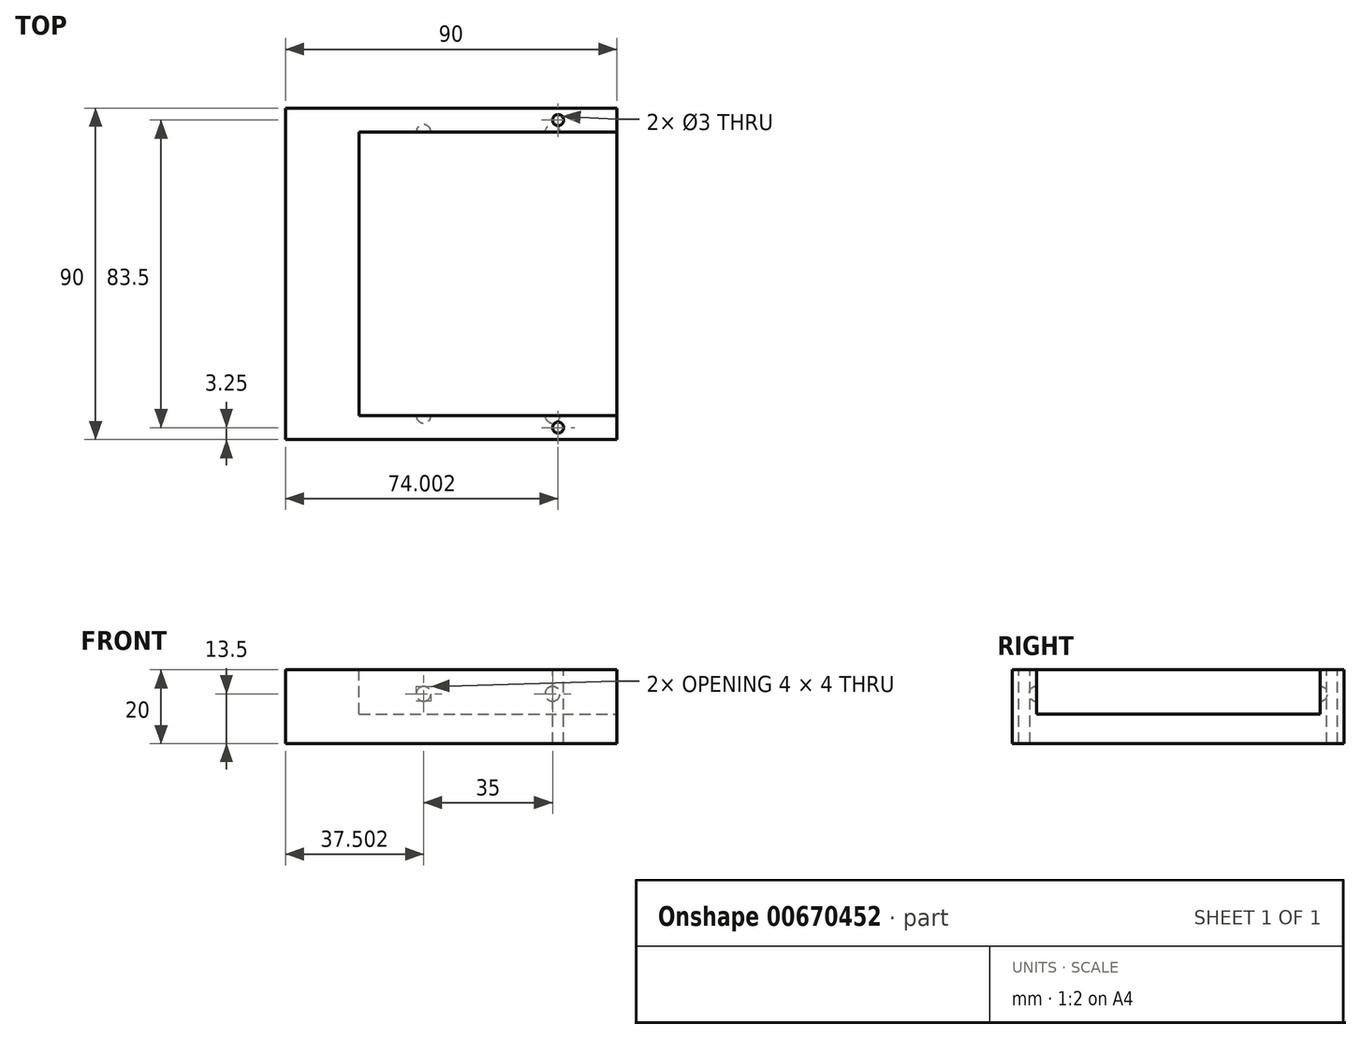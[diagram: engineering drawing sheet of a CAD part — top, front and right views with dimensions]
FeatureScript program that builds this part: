
annotation { "Feature Type Name" : "Feature", "Feature Type Description" : "" }
export const myFeature = defineFeature(function(context is Context, id is Id, definition is map)
    precondition{}
    {
        {
            var Q0;
            Q0=qCreatedBy(makeId("Top.planeOp"),FACE);
            var sketch = newSketch(context, id + "F0", { "sketchPlane" : qUnion([Q0])});
            skPoint(sketch, "E0.middle", {"position": v(0, 0) * mm});
            skLineSegment(sketch, "E1.0", {"start": v(20.17, 45) * mm, "end": v(-69.83, 45) * mm});
            skLineSegment(sketch, "E1.1", {"start": v(20.17, -45) * mm, "end": v(20.17, 45) * mm});
            skLineSegment(sketch, "E1.2", {"start": v(20.17, -45) * mm, "end": v(-69.83, -45) * mm});
            skLineSegment(sketch, "E1.3", {"start": v(-69.83, -45) * mm, "end": v(-69.83, 45) * mm});
            skPoint(sketch, "E0.right.end.orphan", {"position": v(-54.31, 29.48) * mm});
            skPoint(sketch, "E0.bottom.end.orphan", {"position": v(-54.31, -29.48) * mm});
            skPoint(sketch, "E0.left.end.orphan", {"position": v(54.31, 29.48) * mm});
            skPoint(sketch, "E0.left.start.orphan", {"position": v(54.31, -29.48) * mm});
            skSolve(sketch);
        }
        {
            var Q0;
            Q0 = qSketchRegion(id + "F0", true);
            extrude(context, id + "F1", {"entities" : qUnion([Q0]), "depth" : 20 * mm, "offsetDistance" : 25 * mm});
        }
        {
            var Q0;
            Q0=makeQuery(id+"F1.opExtrude","CAP_FACE",FACE,{"disambiguationData":[OSD([sQuery(id+"F0.wireOp",EDGE,"E1.0"),sQuery(id+"F0.wireOp",EDGE,"E1.1"),sQuery(id+"F0.wireOp",EDGE,"E1.2"),sQuery(id+"F0.wireOp",EDGE,"E1.3")])],"isStart":false});
            var sketch = newSketch(context, id + "F2", { "sketchPlane" : qUnion([Q0])});
            skLineSegment(sketch, "E2.bottom", {"start": v(-49.83, -38.5) * mm, "end": v(20.17, -38.5) * mm});
            skLineSegment(sketch, "E2.top", {"start": v(-49.83, 38.5) * mm, "end": v(20.17, 38.5) * mm});
            skLineSegment(sketch, "E2.left", {"start": v(-49.83, -38.5) * mm, "end": v(-49.83, 38.5) * mm});
            skLineSegment(sketch, "E2.right", {"start": v(20.17, -38.5) * mm, "end": v(20.17, 38.5) * mm});
            skLineSegment(sketch, "E3.bottom", {"start": v(-49.83, 38.5) * mm, "end": v(-49.83, 38.5) * mm});
            skLineSegment(sketch, "E3.top", {"start": v(-49.83, -38.5) * mm, "end": v(-49.83, -38.5) * mm});
            skLineSegment(sketch, "E3.left", {"start": v(-49.83, 38.5) * mm, "end": v(-49.83, -38.5) * mm});
            skLineSegment(sketch, "E3.right", {"start": v(-49.83, 38.5) * mm, "end": v(-49.83, -38.5) * mm});
            skPoint(sketch, "E4.right.end.orphan", {"position": v(-66.92, -38.5) * mm});
            skSolve(sketch);
        }
        {
            var Q0;
            Q0 = qSketchRegion(id + "F2", true);
            extrude(context, id + "F3", {"entities" : qUnion([Q0]), "operationType" : NewBodyOperationType.REMOVE, "oppositeDirection" : true, "depth" : 12 * mm, "offsetDistance" : 25 * mm});
        }
        {
            var Q0;
            Q0=makeQuery(id+"F3.boolean.opBoolean","COPY",FACE,{"derivedFrom":makeQuery(id+"F3.opExtrude","SWEPT_FACE",FACE,{"disambiguationData":[OSD([sQuery(id+"F2.wireOp",EDGE,"E2.bottom"),sQuery(id+"F2.wireOp",EDGE,"E4.top")])]})});
            var sketch = newSketch(context, id + "F4", { "sketchPlane" : qUnion([Q0])});
            skArc(sketch, "E5", {"start": v(32.33, 15.5) * mm, "mid": v(30.33, 13.5) * mm, "end": v(32.33, 11.5) * mm});
            skLineSegment(sketch, "E6", {"start": v(32.33, 11.5) * mm, "end": v(32.33, 15.5) * mm});
            skSolve(sketch);
        }
        {
            var Q0;
            Q0=makeQuery(id+"F4.imprint","IMPRINT",FACE,{"disambiguationData":[TD([[makeQuery(id+"F4.imprint","IMPRINT",EDGE,{"derivedFrom":sQuery(id+"F4.wireOp",EDGE,"E5")}),1.0]])]});
            var Q1;
            Q1=sQuery(id+"F4.wireOp",EDGE,"CeXaYvnH-7o9a-OPG4-3ZQA-x74nUvsMlTij");
            var Q2;
            Q2=sQuery(id+"F4.wireOp",EDGE,"vrGOqkmy-BDjh-gprZ-iLit-p3grwdgPlS82");
            var Q3;
            Q3=sQuery(id+"F4.wireOp",EDGE,"E6");
            revolve(context, id + "F5", {"operationType" : NewBodyOperationType.REMOVE, "entities" : qUnion([Q0]), "surfaceEntities" : qUnion([Q1, Q2]), "axis" : qUnion([Q3]), "revolveType" : RevolveType.FULL, "oppositeDirection" : true});
        }
        {
            var Q0;
            Q0=makeQuery(id+"F3.boolean.opBoolean","COPY",FACE,{"derivedFrom":makeQuery(id+"F3.opExtrude","SWEPT_FACE",FACE,{"disambiguationData":[OSD([sQuery(id+"F2.wireOp",EDGE,"E2.bottom"),sQuery(id+"F2.wireOp",EDGE,"E4.top")])]})});
            var sketch = newSketch(context, id + "F6", { "sketchPlane" : qUnion([Q0])});
            skArc(sketch, "E7", {"start": v(-2.67, 15.5) * mm, "mid": v(-4.67, 13.5) * mm, "end": v(-2.67, 11.5) * mm});
            skLineSegment(sketch, "E8", {"start": v(-2.67, 11.5) * mm, "end": v(-2.67, 15.5) * mm});
            skSolve(sketch);
        }
        {
            var Q0;
            Q0=makeQuery(id+"F6.imprint","IMPRINT",FACE,{"disambiguationData":[TD([[makeQuery(id+"F6.imprint","IMPRINT",EDGE,{"derivedFrom":sQuery(id+"F6.wireOp",EDGE,"E7")}),1.0]])]});
            var Q1;
            Q1=sQuery(id+"F6.wireOp",EDGE,"E8");
            revolve(context, id + "F7", {"operationType" : NewBodyOperationType.REMOVE, "entities" : qUnion([Q0]), "axis" : qUnion([Q1]), "revolveType" : RevolveType.FULL, "oppositeDirection" : true});
        }
        {
            var Q0;
            Q0=makeQuery(id+"F3.boolean.opBoolean","COPY",FACE,{"derivedFrom":makeQuery(id+"F3.opExtrude","SWEPT_FACE",FACE,{"disambiguationData":[OSD([sQuery(id+"F2.wireOp",EDGE,"E2.top"),sQuery(id+"F2.wireOp",EDGE,"E4.bottom")])]})});
            var sketch = newSketch(context, id + "F8", { "sketchPlane" : qUnion([Q0])});
            skArc(sketch, "E9", {"start": v(2.67, 11.5) * mm, "mid": v(4.67, 13.5) * mm, "end": v(2.67, 15.5) * mm});
            skLineSegment(sketch, "E10", {"start": v(2.67, 11.5) * mm, "end": v(2.67, 15.5) * mm});
            skSolve(sketch);
        }
        {
            var Q0;
            Q0=makeQuery(id+"F8.imprint","IMPRINT",FACE,{"disambiguationData":[TD([[makeQuery(id+"F8.imprint","IMPRINT",EDGE,{"derivedFrom":sQuery(id+"F8.wireOp",EDGE,"E9")}),1.0]])]});
            var Q1;
            Q1=sQuery(id+"F8.wireOp",EDGE,"E10");
            revolve(context, id + "F9", {"operationType" : NewBodyOperationType.REMOVE, "entities" : qUnion([Q0]), "axis" : qUnion([Q1]), "revolveType" : RevolveType.FULL, "oppositeDirection" : true});
        }
        {
            var Q0;
            Q0=makeQuery(id+"F3.boolean.opBoolean","COPY",FACE,{"derivedFrom":makeQuery(id+"F3.opExtrude","SWEPT_FACE",FACE,{"disambiguationData":[OSD([sQuery(id+"F2.wireOp",EDGE,"E2.top"),sQuery(id+"F2.wireOp",EDGE,"E4.bottom")])]})});
            var sketch = newSketch(context, id + "F10", { "sketchPlane" : qUnion([Q0])});
            skArc(sketch, "E11", {"start": v(-32.33, 15.5) * mm, "mid": v(-34.33, 13.5) * mm, "end": v(-32.33, 11.5) * mm});
            skLineSegment(sketch, "E12", {"start": v(-32.33, 11.5) * mm, "end": v(-32.33, 15.5) * mm});
            skSolve(sketch);
        }
        {
            var Q0;
            Q0=makeQuery(id+"F10.imprint","IMPRINT",FACE,{"disambiguationData":[TD([[makeQuery(id+"F10.imprint","IMPRINT",EDGE,{"derivedFrom":sQuery(id+"F10.wireOp",EDGE,"E11")}),1.0]])]});
            var Q1;
            Q1=sQuery(id+"F10.wireOp",EDGE,"E12");
            revolve(context, id + "F11", {"operationType" : NewBodyOperationType.REMOVE, "entities" : qUnion([Q0]), "axis" : qUnion([Q1]), "revolveType" : RevolveType.FULL, "oppositeDirection" : true});
        }
        {
            var Q0;
            Q0=makeQuery(id+"F1.opExtrude","CAP_FACE",FACE,{"disambiguationData":[OSD([sQuery(id+"F0.wireOp",EDGE,"E1.0"),sQuery(id+"F0.wireOp",EDGE,"E1.1"),sQuery(id+"F0.wireOp",EDGE,"E1.2"),sQuery(id+"F0.wireOp",EDGE,"E1.3")])],"isStart":false});
            var sketch = newSketch(context, id + "F12", { "sketchPlane" : qUnion([Q0])});
            skPoint(sketch, "E13.right.end.orphan", {"position": v(13.67, -38.5) * mm});
            skCircle(sketch, "E14", {"center": v(4.17, -41.75) * mm, "radius": 1.5 * mm});
            skCircle(sketch, "E15", {"center": v(4.17, 41.75) * mm, "radius": 1.5 * mm});
            skPoint(sketch, "E16.top.end.orphan", {"position": v(13.67, 38.5) * mm});
            skSolve(sketch);
        }
        {
            var Q0;
            Q0 = qSketchRegion(id + "F12", true);
            extrude(context, id + "F13", {"entities" : qUnion([Q0]), "operationType" : NewBodyOperationType.REMOVE, "oppositeDirection" : true, "depth" : 25 * mm, "offsetDistance" : 25 * mm});
        }
    });
